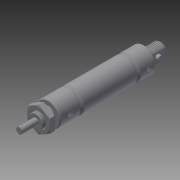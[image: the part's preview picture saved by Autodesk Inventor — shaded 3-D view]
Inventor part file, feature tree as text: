
AUTODESK INVENTOR PART (.ipt)
format: ipt  version: 2014 (Build 180170000, 170)  size: 1,159,680 bytes
history: native  units: in
note: dims shown in document units (in); Inventor stores cm internally (conversion verified against a paired STEP export)
features: other x5, imported_body x4, extrude x1, sketch x1
ambient origin geometry x8: Origin, YZ Plane, XZ Plane, XY Plane, X Axis, Y Axis, Z Axis, Center Point
bodies: Body1 (feature_tree), Body2 (feature_tree), Body3 (feature_tree), Body4 (feature_tree)
feature tree (11):
  parser-record x1  (decoder bookkeeping rows leaked as tree rows — omitted from the tree; the rows remain in map.json)
  other  "6498K6021"
  extrude  "Extrusion1"  [1 undecoded]
  other  "NONE_1"
  other  "NONE_2"
  other  "NONE_3"
  imported_body  "Base1"
  imported_body  "Base2"
  imported_body  "Base3"
  imported_body  "Base4"
  sketch  "Sketch1"  dims[d0=1.0in d1=0.0in]
note: 1 required parameter value undecoded (feature->parameter linkage not recoverable at this tier; creation-order binding heuristic only, values carry confidence <= 0.55)
